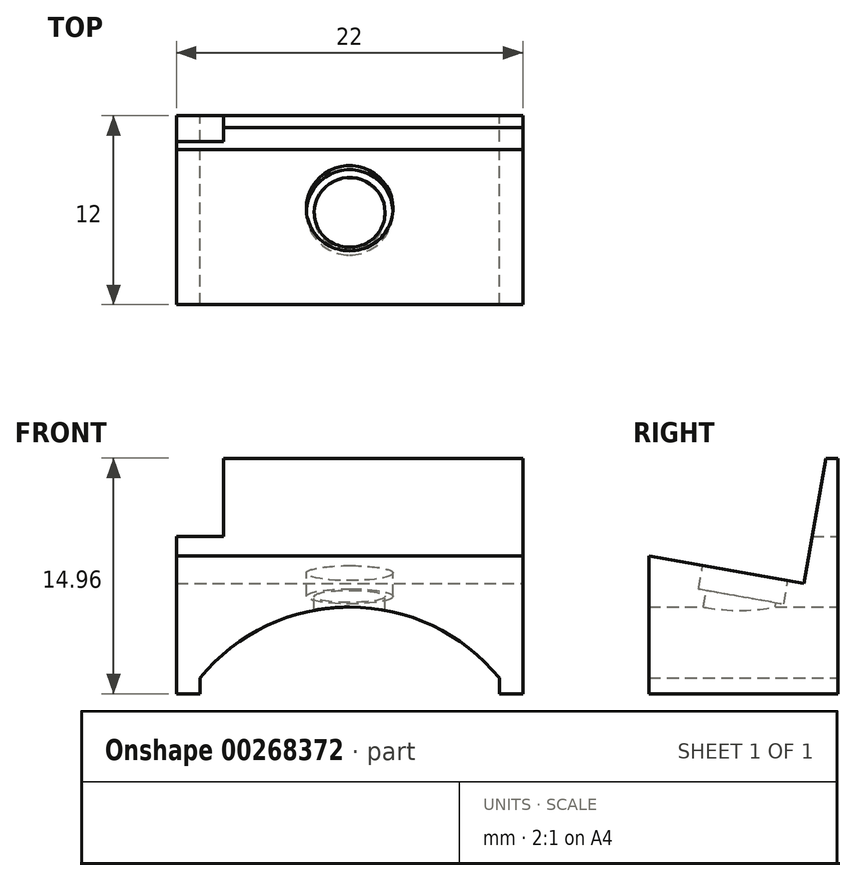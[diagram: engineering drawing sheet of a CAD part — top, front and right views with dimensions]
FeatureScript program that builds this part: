
annotation { "Feature Type Name" : "Feature", "Feature Type Description" : "" }
export const myFeature = defineFeature(function(context is Context, id is Id, definition is map)
    precondition{}
    {
        {
            var Q0;
            Q0=qCreatedBy(makeId("Front.planeOp"),FACE);
            var sketch = newSketch(context, id + "F0", { "sketchPlane" : qUnion([Q0])});
            skArc(sketch, "E0", {"start": v(9.5, 6.11) * mm, "mid": v(0, 10.61) * mm, "end": v(-9.5, 6.11) * mm});
            skLineSegment(sketch, "E1", {"start": v(0, 10.61) * mm, "end": v(16.3, 10.61) * mm, "construction": true});
            skLineSegment(sketch, "E2", {"start": v(16.3, 10.61) * mm, "end": v(16.3, 6.11) * mm, "construction": true});
            skLineSegment(sketch, "E3", {"start": v(16.3, 6.11) * mm, "end": v(9.5, 6.11) * mm, "construction": true});
            skLineSegment(sketch, "E4", {"start": v(-9.5, 6.11) * mm, "end": v(-11, 6.11) * mm});
            skLineSegment(sketch, "E5", {"start": v(-11, 6.11) * mm, "end": v(-11, 21.11) * mm});
            skLineSegment(sketch, "E6", {"start": v(-11, 21.11) * mm, "end": v(11, 21.11) * mm});
            skLineSegment(sketch, "E7", {"start": v(11, 21.11) * mm, "end": v(11, 6.11) * mm});
            skLineSegment(sketch, "E8", {"start": v(11, 6.11) * mm, "end": v(9.5, 6.11) * mm});
            skSolve(sketch);
        }
        {
            var Q0;
            Q0 = qSketchRegion(id + "F0", true);
            extrude(context, id + "F1", {"entities" : qUnion([Q0]), "depth" : 12 * mm});
        }
        {
            var Q0;
            Q0=makeQuery(id+"F1.opExtrude","SWEPT_FACE",FACE,{"disambiguationData":[OSD([sQuery(id+"F0.wireOp",EDGE,"E7")])]});
            var sketch = newSketch(context, id + "F2", { "sketchPlane" : qUnion([Q0])});
            skLineSegment(sketch, "E9", {"start": v(-12, 13.85) * mm, "end": v(-2.15, 12.11) * mm});
            skLineSegment(sketch, "E10", {"start": v(-2.15, 12.11) * mm, "end": v(-0.75, 20.07) * mm});
            skLineSegment(sketch, "E11", {"start": v(-0.75, 20.07) * mm, "end": v(0, 20.07) * mm});
            skLineSegment(sketch, "E12", {"start": v(0, 20.07) * mm, "end": v(0, 21.11) * mm});
            skLineSegment(sketch, "E13", {"start": v(0, 21.11) * mm, "end": v(-12, 21.11) * mm});
            skLineSegment(sketch, "E14", {"start": v(-12, 21.11) * mm, "end": v(-12, 13.85) * mm});
            skLineSegment(sketch, "E15", {"start": v(-2.15, 12.11) * mm, "end": v(-12, 12.11) * mm, "construction": true});
            skSolve(sketch);
        }
        {
            var Q0;
            Q0 = qSketchRegion(id + "F2", true);
            extrude(context, id + "F3", {"entities" : qUnion([Q0]), "operationType" : NewBodyOperationType.REMOVE, "endBound" : BoundingType.THROUGH_ALL, "oppositeDirection" : true, "depth" : 25 * mm});
        }
        {
            var Q0;
            Q0=makeQuery(id+"F1.opExtrude","SWEPT_FACE",FACE,{"disambiguationData":[OSD([sQuery(id+"F0.wireOp",EDGE,"E5")])]});
            var sketch = newSketch(context, id + "F4", { "sketchPlane" : qUnion([Q0])});
            skLineSegment(sketch, "E16", {"start": v(0, 20.07) * mm, "end": v(0.75, 20.07) * mm});
            skLineSegment(sketch, "E17", {"start": v(0.75, 20.07) * mm, "end": v(1.62, 15.11) * mm});
            skLineSegment(sketch, "E18", {"start": v(1.62, 15.11) * mm, "end": v(0, 15.11) * mm});
            skLineSegment(sketch, "E19", {"start": v(0, 15.11) * mm, "end": v(0, 20.07) * mm});
            skSolve(sketch);
        }
        {
            var Q0;
            Q0 = qSketchRegion(id + "F4", true);
            extrude(context, id + "F5", {"entities" : qUnion([Q0]), "operationType" : NewBodyOperationType.REMOVE, "oppositeDirection" : true, "depth" : 3 * mm});
        }
        {
            var Q0;
            Q0=makeQuery(id+"F1.opExtrude","SWEPT_FACE",FACE,{"disambiguationData":[OSD([sQuery(id+"F0.wireOp",EDGE,"E4")])]});
            var sketch = newSketch(context, id + "F6", { "sketchPlane" : qUnion([Q0])});
            skLineSegment(sketch, "E20.bottom", {"start": v(-11, 12) * mm, "end": v(-9.5, 12) * mm});
            skLineSegment(sketch, "E20.top", {"start": v(-11, 0) * mm, "end": v(-9.5, 0) * mm});
            skLineSegment(sketch, "E20.left", {"start": v(-11, 12) * mm, "end": v(-11, 0) * mm});
            skLineSegment(sketch, "E20.right", {"start": v(-9.5, 12) * mm, "end": v(-9.5, 0) * mm});
            skSolve(sketch);
        }
        {
            var Q0;
            Q0 = qSketchRegion(id + "F6", true);
            extrude(context, id + "F7", {"entities" : qUnion([Q0]), "operationType" : NewBodyOperationType.ADD, "depth" : 1 * mm});
        }
        {
            var Q0;
            Q0=makeQuery(id+"F1.opExtrude","SWEPT_FACE",FACE,{"disambiguationData":[OSD([sQuery(id+"F0.wireOp",EDGE,"E8")])]});
            var sketch = newSketch(context, id + "F8", { "sketchPlane" : qUnion([Q0])});
            skLineSegment(sketch, "E21.bottom", {"start": v(9.5, 12) * mm, "end": v(11, 12) * mm});
            skLineSegment(sketch, "E21.top", {"start": v(9.5, 0) * mm, "end": v(11, 0) * mm});
            skLineSegment(sketch, "E21.left", {"start": v(9.5, 12) * mm, "end": v(9.5, 0) * mm});
            skLineSegment(sketch, "E21.right", {"start": v(11, 12) * mm, "end": v(11, 0) * mm});
            skSolve(sketch);
        }
        {
            var Q0;
            Q0 = qSketchRegion(id + "F8", true);
            extrude(context, id + "F9", {"entities" : qUnion([Q0]), "operationType" : NewBodyOperationType.ADD, "depth" : 1 * mm});
        }
        {
            var Q0;
            Q0=makeQuery(id+"F3.boolean.opBoolean","COPY",FACE,{"derivedFrom":makeQuery(id+"F3.opExtrude","SWEPT_FACE",FACE,{"disambiguationData":[OSD([sQuery(id+"F2.wireOp",EDGE,"E9")])]})});
            var sketch = newSketch(context, id + "F10", { "sketchPlane" : qUnion([Q0])});
            skCircle(sketch, "E22", {"center": v(0, -8) * mm, "radius": 2.75 * mm});
            skSolve(sketch);
        }
        {
            var Q0;
            Q0 = qSketchRegion(id + "F10", true);
            extrude(context, id + "F11", {"entities" : qUnion([Q0]), "operationType" : NewBodyOperationType.REMOVE, "oppositeDirection" : true, "depth" : 1.5 * mm});
        }
        {
            var Q0;
            Q0=makeQuery(id+"F11.boolean.opBoolean","COPY",FACE,{"derivedFrom":makeQuery(id+"F11.opExtrude","CAP_FACE",FACE,{"disambiguationData":[OSD([sQuery(id+"F10.wireOp",EDGE,"E22")])],"isStart":false})});
            var sketch = newSketch(context, id + "F12", { "sketchPlane" : qUnion([Q0])});
            skCircle(sketch, "E23", {"center": v(0, -8) * mm, "radius": 2.25 * mm});
            skSolve(sketch);
        }
        {
            var Q0;
            Q0 = qSketchRegion(id + "F12", true);
            extrude(context, id + "F13", {"entities" : qUnion([Q0]), "operationType" : NewBodyOperationType.REMOVE, "oppositeDirection" : true, "depth" : 25 * mm});
        }
    });
